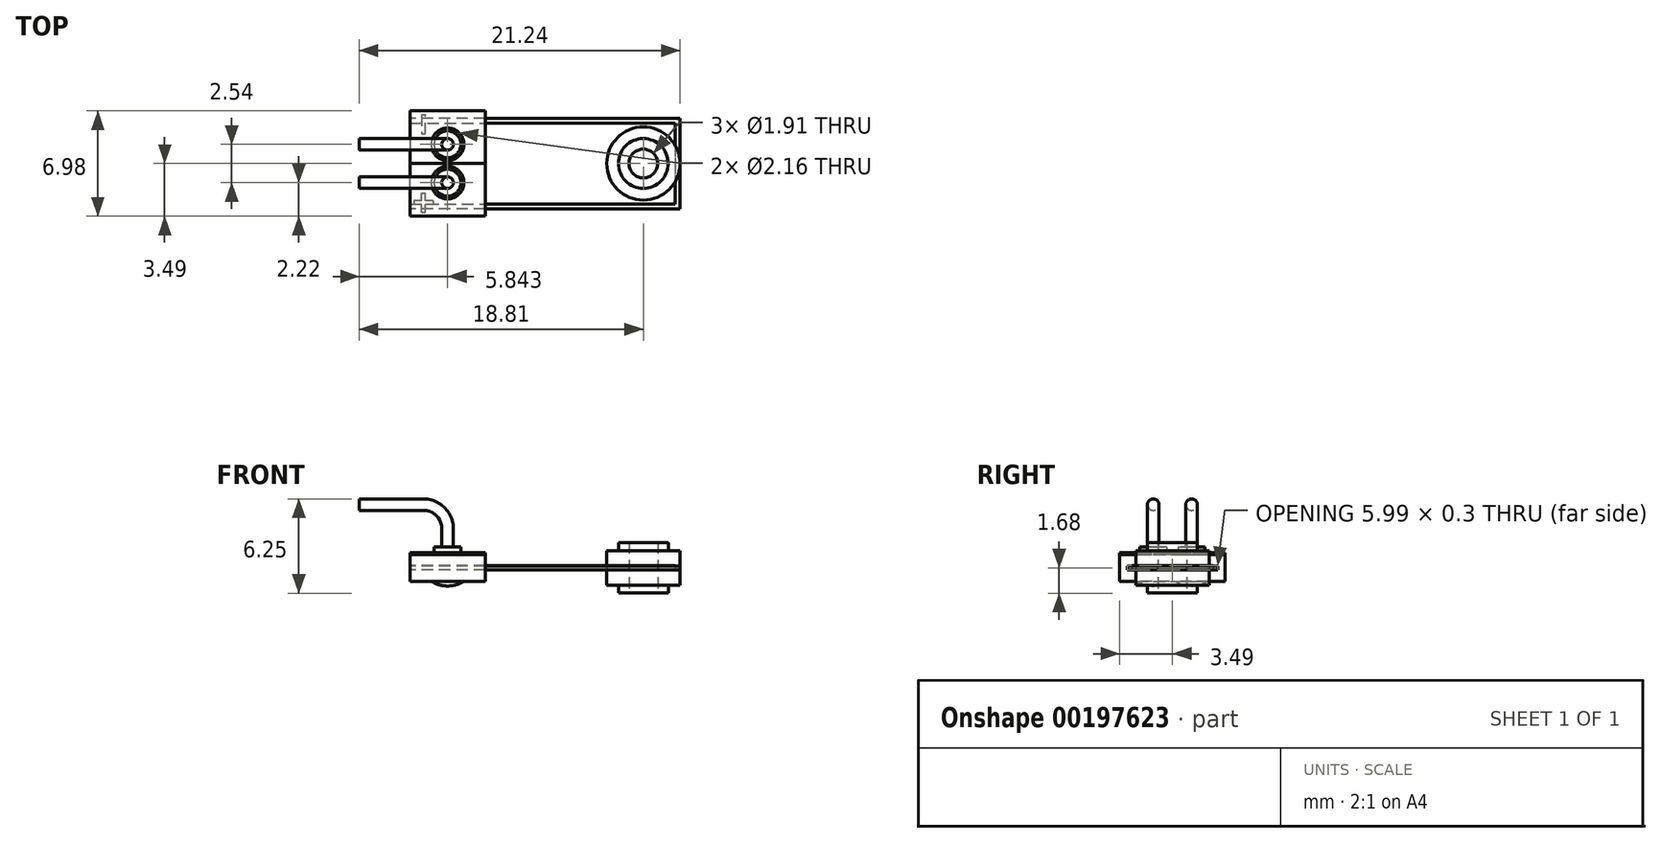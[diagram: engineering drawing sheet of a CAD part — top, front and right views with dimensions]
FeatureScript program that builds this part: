
annotation { "Feature Type Name" : "Feature", "Feature Type Description" : "" }
export const myFeature = defineFeature(function(context is Context, id is Id, definition is map)
    precondition{}
    {
        {
            var Q0;
            Q0=qCreatedBy(makeId("Top.planeOp"),FACE);
            var sketch = newSketch(context, id + "F0", { "sketchPlane" : qUnion([Q0])});
            skCircle(sketch, "E0", {"center": v(0, 0) * mm, "radius": 2.43 * mm});
            skCircle(sketch, "E1", {"center": v(0, 0) * mm, "radius": 1.65 * mm});
            skCircle(sketch, "E2", {"center": v(0, 0) * mm, "radius": 0.95 * mm});
            skSolve(sketch);
        }
        {
            var Q0;
            Q0=makeQuery(id+"F0.imprint","IMPRINT",FACE,{"disambiguationData":[TD([[makeQuery(id+"F0.imprint","IMPRINT",EDGE,{"derivedFrom":sQuery(id+"F0.wireOp",EDGE,"E0")}),1.0]])]});
            var Q1;
            Q1=makeQuery(id+"F0.imprint","IMPRINT",FACE,{"disambiguationData":[TD([[makeQuery(id+"F0.imprint","IMPRINT",EDGE,{"derivedFrom":sQuery(id+"F0.wireOp",EDGE,"E1")}),1.0]])]});
            extrude(context, id + "F1", {"entities" : qUnion([Q0, Q1]), "depth" : 1.14 * mm, "hasSecondDirection" : true, "secondDirectionOppositeDirection" : true, "secondDirectionDepth" : 1.14 * mm});
        }
        {
            var Q0;
            Q0=makeQuery(id+"F0.imprint","IMPRINT",FACE,{"disambiguationData":[TD([[makeQuery(id+"F0.imprint","IMPRINT",EDGE,{"derivedFrom":sQuery(id+"F0.wireOp",EDGE,"E1")}),1.0]])]});
            var Q1;
            Q1=sQuery(id+"F0.wireOp",EDGE,"E1");
            var Q2;
            Q2=sQuery(id+"F0.wireOp",EDGE,"E2");
            extrude(context, id + "F2", {"entities" : qUnion([Q0]), "operationType" : NewBodyOperationType.ADD, "surfaceEntities" : qUnion([Q1, Q2]), "endBound" : BoundingType.SYMMETRIC, "depth" : 3.35 * mm});
        }
        {
            var Q0;
            Q0=qCreatedBy(makeId("Top.planeOp"),FACE);
            var sketch = newSketch(context, id + "F3", { "sketchPlane" : qUnion([Q0])});
            skPoint(sketch, "E3", {"position": v(2.43, 0) * mm});
            skLineSegment(sketch, "E4.bottom", {"start": v(2.43, -3) * mm, "end": v(-15.46, -3) * mm});
            skLineSegment(sketch, "E4.top", {"start": v(2.43, 3) * mm, "end": v(-15.46, 3) * mm});
            skLineSegment(sketch, "E4.left", {"start": v(2.43, -3) * mm, "end": v(2.43, 3) * mm});
            skLineSegment(sketch, "E4.right", {"start": v(-15.46, -3) * mm, "end": v(-15.46, 3) * mm});
            skPoint(sketch, "E4.middle", {"position": v(-6.52, 0) * mm});
            skSolve(sketch);
        }
        {
            var Q0;
            Q0 = qSketchRegion(id + "F3", true);
            extrude(context, id + "F4", {"entities" : qUnion([Q0]), "endBound" : BoundingType.SYMMETRIC, "depth" : 0.25 * mm});
        }
        {
            var Q0;
            Q0=qCreatedBy(makeId("Top.planeOp"),FACE);
            var sketch = newSketch(context, id + "F5", { "sketchPlane" : qUnion([Q0])});
            skLineSegment(sketch, "E5.bottom", {"start": v(2.1, 2.68) * mm, "end": v(-15.46, 2.68) * mm});
            skLineSegment(sketch, "E5.top", {"start": v(2.1, -2.68) * mm, "end": v(-15.46, -2.68) * mm});
            skLineSegment(sketch, "E5.left", {"start": v(2.1, 2.68) * mm, "end": v(2.1, -2.68) * mm});
            skLineSegment(sketch, "E5.right", {"start": v(-15.46, 2.68) * mm, "end": v(-15.46, -2.68) * mm});
            skPoint(sketch, "E5.middle", {"position": v(-6.67, 0) * mm});
            skSolve(sketch);
        }
        {
            var Q0;
            Q0 = qSketchRegion(id + "F5", true);
            extrude(context, id + "F6", {"entities" : qUnion([Q0]), "endBound" : BoundingType.SYMMETRIC, "depth" : 0.3 * mm});
        }
        {
            var Q0;
            Q0=makeQuery(id+"F0.imprint","IMPRINT",FACE,{"disambiguationData":[TD([[makeQuery(id+"F0.imprint","IMPRINT",EDGE,{"derivedFrom":sQuery(id+"F0.wireOp",EDGE,"E2")}),1.0]])]});
            extrude(context, id + "F7", {"entities" : qUnion([Q0]), "operationType" : NewBodyOperationType.REMOVE, "endBound" : BoundingType.SYMMETRIC, "oppositeDirection" : true, "depth" : 25.4 * mm});
        }
        {
            var Q0;
            Q0=qCreatedBy(makeId("Top.planeOp"),FACE);
            var sketch = newSketch(context, id + "F8", { "sketchPlane" : qUnion([Q0])});
            skPoint(sketch, "E6.0", {"position": v(-15.46, 0) * mm});
            skLineSegment(sketch, "E7.bottom", {"start": v(-15.46, -3.5) * mm, "end": v(-10.48, -3.5) * mm});
            skLineSegment(sketch, "E7.top", {"start": v(-15.46, 3.5) * mm, "end": v(-10.48, 3.5) * mm});
            skLineSegment(sketch, "E7.left", {"start": v(-15.46, -3.5) * mm, "end": v(-15.46, 3.5) * mm});
            skLineSegment(sketch, "E7.right", {"start": v(-10.48, -3.5) * mm, "end": v(-10.48, 3.5) * mm});
            skPoint(sketch, "E7.middle", {"position": v(-12.97, 0) * mm});
            skSolve(sketch);
        }
        {
            var Q0;
            Q0=makeQuery(id+"F8.imprint","IMPRINT",FACE,{"disambiguationData":[TD([[makeQuery(id+"F8.imprint","IMPRINT",EDGE,{"derivedFrom":sQuery(id+"F8.wireOp",EDGE,"E7.bottom")}),1.0]])]});
            extrude(context, id + "F9", {"entities" : qUnion([Q0]), "endBound" : BoundingType.SYMMETRIC, "depth" : 1.78 * mm});
        }
        {
            var Q0;
            Q0=makeQuery(id+"F4.opExtrude","SWEPT_BODY",BODY,{"disambiguationData":[OSD([sQuery(id+"F3.wireOp",EDGE,"E4.bottom"),sQuery(id+"F3.wireOp",EDGE,"E4.top"),sQuery(id+"F3.wireOp",EDGE,"E4.left"),sQuery(id+"F3.wireOp",EDGE,"E4.right")])]});
            var Q1;
            Q1=makeQuery(id+"F6.opExtrude","SWEPT_BODY",BODY,{"disambiguationData":[OSD([sQuery(id+"F5.wireOp",EDGE,"E5.bottom"),sQuery(id+"F5.wireOp",EDGE,"E5.top"),sQuery(id+"F5.wireOp",EDGE,"E5.left"),sQuery(id+"F5.wireOp",EDGE,"E5.right")])]});
            var Q2;
            Q2=makeQuery(id+"F9.opExtrude","SWEPT_BODY",BODY,{"disambiguationData":[OSD([sQuery(id+"F8.wireOp",EDGE,"E7.bottom"),sQuery(id+"F8.wireOp",EDGE,"E7.top"),sQuery(id+"F8.wireOp",EDGE,"E7.left"),sQuery(id+"F8.wireOp",EDGE,"E7.right")])]});
            booleanBodies(context, id + "F10", {"operationType" : BooleanOperationType.SUBTRACTION, "tools" : qUnion([Q0, Q1]), "targets" : qUnion([Q2]), "keepTools" : true});
        }
        {
            var Q0;
            Q0=makeQuery(id+"F9.opExtrude","CAP_FACE",FACE,{"disambiguationData":[OSD([sQuery(id+"F8.wireOp",EDGE,"E7.bottom"),sQuery(id+"F8.wireOp",EDGE,"E7.top"),sQuery(id+"F8.wireOp",EDGE,"E7.left"),sQuery(id+"F8.wireOp",EDGE,"E7.right")])],"isStart":true});
            var sketch = newSketch(context, id + "F11", { "sketchPlane" : qUnion([Q0])});
            skPoint(sketch, "E8.0", {"position": v(0, 0) * mm});
            skPoint(sketch, "E9.0", {"position": v(-15.46, 0) * mm});
            skCircle(sketch, "E10.0", {"center": v(0, 0) * mm, "radius": 2.43 * mm});
            skPoint(sketch, "E11.middle", {"position": v(-12.97, 0) * mm});
            skPoint(sketch, "E11.middle.positionSnap0", {"position": v(-10.48, 0) * mm});
            skPoint(sketch, "E11.centerSnap0", {"position": v(-10.48, 0) * mm});
            skLineSegment(sketch, "E12", {"start": v(-15.46, 0) * mm, "end": v(-10.48, 0) * mm});
            skCircle(sketch, "E13", {"center": v(-12.97, 1.27) * mm, "radius": 1.08 * mm});
            skPoint(sketch, "E13.centerSnap0", {"position": v(-12.97, 0.25) * mm});
            skSolve(sketch);
        }
        {
            var Q0;
            Q0=qCreatedBy(makeId("Front.planeOp"),FACE);
            cPlane(context, id + "F12", {"entities" : qUnion([Q0]), "cplaneType" : CPlaneType.OFFSET, "offset" : 1.27 * mm, "width" : 152.4 * mm, "height" : 152.4 * mm});
        }
        {
            var Q0;
            Q0=qCreatedBy(id+"F12.planeOp",FACE);
            var sketch = newSketch(context, id + "F13", { "sketchPlane" : qUnion([Q0])});
            skLineSegment(sketch, "E14.0.0", {"start": v(-12.97, -0.89) * mm, "end": v(-14.05, -0.89) * mm});
            skArc(sketch, "E15", {"start": v(-14.05, -0.89) * mm, "mid": v(-13.53, -1.13) * mm, "end": v(-12.97, -1.2) * mm});
            skLineSegment(sketch, "E16", {"start": v(-12.97, -0.89) * mm, "end": v(-12.97, -1.2) * mm});
            skPoint(sketch, "E17.orphan", {"position": v(-11.89, -0.89) * mm});
            skSolve(sketch);
        }
        {
            var Q0;
            Q0 = qSketchRegion(id + "F13", true);
            var Q1;
            Q1=sQuery(id+"F13.wireOp",EDGE,"E16");
            revolve(context, id + "F14", {"entities" : qUnion([Q0]), "axis" : qUnion([Q1]), "revolveType" : RevolveType.FULL, "oppositeDirection" : true});
        }
        {
            var Q0;
            Q0=makeQuery(id+"F14.opRevolve","SWEPT_BODY",BODY,{"disambiguationData":[OSD([sQuery(id+"F13.wireOp",EDGE,"E14.0.0"),sQuery(id+"F13.wireOp",EDGE,"E15"),sQuery(id+"F13.wireOp",EDGE,"E16")])]});
            var Q1;
            Q1=qCreatedBy(makeId("Front.planeOp"),FACE);
            mirror(context, id + "F15", {"entities" : qUnion([Q0]), "mirrorPlane" : qUnion([Q1])});
        }
        {
            var Q0;
            Q0=makeQuery(id+"F9.opExtrude","CAP_FACE",FACE,{"disambiguationData":[OSD([sQuery(id+"F8.wireOp",EDGE,"E7.bottom"),sQuery(id+"F8.wireOp",EDGE,"E7.top"),sQuery(id+"F8.wireOp",EDGE,"E7.left"),sQuery(id+"F8.wireOp",EDGE,"E7.right")])],"isStart":false});
            var sketch = newSketch(context, id + "F16", { "sketchPlane" : qUnion([Q0])});
            skCircle(sketch, "E18.0", {"center": v(-12.97, -1.27) * mm, "radius": 1.08 * mm});
            skLineSegment(sketch, "E19.0", {"start": v(-15.46, 0) * mm, "end": v(-10.48, 0) * mm});
            skCircle(sketch, "E20", {"center": v(-12.97, -1.27) * mm, "radius": 0.89 * mm});
            skCircle(sketch, "E21", {"center": v(-12.97, -1.27) * mm, "radius": 0.5 * mm});
            skPoint(sketch, "E22", {"position": v(-12.46, -1.27) * mm});
            skPoint(sketch, "E23", {"position": v(-12.46, 0) * mm});
            skLineSegment(sketch, "E24", {"start": v(-12.46, -1.27) * mm, "end": v(-12.46, 0) * mm});
            skLineSegment(sketch, "E25", {"start": v(-12.46, -1.27) * mm, "end": v(-12.97, -1.27) * mm});
            skSolve(sketch);
        }
        {
            var Q0;
            Q0=makeQuery(id+"F16.imprint","IMPRINT",FACE,{"disambiguationData":[TD([[makeQuery(id+"F16.imprint","IMPRINT",EDGE,{"derivedFrom":sQuery(id+"F16.wireOp",EDGE,"E18.0")}),-1.0]])]});
            var Q1;
            Q1=makeQuery(id+"F16.imprint","IMPRINT",FACE,{"disambiguationData":[TD([[makeQuery(id+"F16.imprint","IMPRINT",EDGE,{"derivedFrom":sQuery(id+"F16.wireOp",EDGE,"E20")}),1.0]])]});
            var Q2;
            Q2=makeQuery(id+"F16.imprint","IMPRINT",FACE,{"disambiguationData":[TD([[makeQuery(id+"F16.imprint","IMPRINT",EDGE,{"derivedFrom":sQuery(id+"F16.wireOp",EDGE,"E21")}),1.0]])]});
            var Q3;
            Q3=sQuery(id+"F16.wireOp",EDGE,"E18.0");
            extrude(context, id + "F17", {"entities" : qUnion([Q0, Q1, Q2]), "surfaceEntities" : qUnion([Q3]), "depth" : 0.13 * mm});
        }
        {
            var Q0;
            Q0=makeQuery(id+"F17.opExtrude","SWEPT_BODY",BODY,{"disambiguationData":[OSD([sQuery(id+"F16.wireOp",EDGE,"E18.0")])]});
            var Q1;
            Q1=qCreatedBy(makeId("Front.planeOp"),FACE);
            mirror(context, id + "F18", {"entities" : qUnion([Q0]), "mirrorPlane" : qUnion([Q1])});
        }
        {
            var Q0;
            Q0=makeQuery(id+"F16.imprint","IMPRINT",FACE,{"disambiguationData":[TD([[makeQuery(id+"F16.imprint","IMPRINT",EDGE,{"derivedFrom":sQuery(id+"F16.wireOp",EDGE,"E20")}),1.0]])]});
            var Q1;
            Q1=makeQuery(id+"F16.imprint","IMPRINT",FACE,{"disambiguationData":[TD([[makeQuery(id+"F16.imprint","IMPRINT",EDGE,{"derivedFrom":sQuery(id+"F16.wireOp",EDGE,"E21")}),1.0]])]});
            extrude(context, id + "F19", {"entities" : qUnion([Q0, Q1]), "depth" : 0.5 * mm});
        }
        {
            var Q0;
            Q0=sQuery(id+"F16.wireOp",EDGE,"E24");
            var Q1;
            Q1=makeQuery(id+"F9.opExtrude","SWEPT_FACE",FACE,{"disambiguationData":[OSD([sQuery(id+"F8.wireOp",EDGE,"E7.left")])]});
            cPlane(context, id + "F20", {"entities" : qUnion([Q0, Q1]), "cplaneType" : CPlaneType.LINE_ANGLE, "offset" : 25.4 * mm, "angle" : 0 * degree, "width" : 152.4 * mm, "height" : 152.4 * mm});
        }
        {
            var Q0;
            Q0=sQuery(id+"F16.wireOp",EDGE,"E25");
            var Q1;
            Q1=qCreatedBy(makeId("Front.planeOp"),FACE);
            cPlane(context, id + "F21", {"entities" : qUnion([Q0, Q1]), "cplaneType" : CPlaneType.LINE_ANGLE, "offset" : 25.4 * mm, "angle" : 0 * degree, "width" : 152.4 * mm, "height" : 152.4 * mm});
        }
        {
            var Q0;
            Q0=qCreatedBy(id+"F21.planeOp",FACE);
            var sketch = newSketch(context, id + "F22", { "sketchPlane" : qUnion([Q0])});
            skPoint(sketch, "E26.0", {"position": v(12.97, 0.79) * mm});
            skLineSegment(sketch, "E27.0", {"start": v(12.08, 1.4) * mm, "end": v(13.86, 1.4) * mm});
            skPoint(sketch, "E28", {"position": v(18.8, 4.2) * mm});
            skPoint(sketch, "E29.endSnap0", {"position": v(12.97, 1.4) * mm});
            skLineSegment(sketch, "E30", {"start": v(18.8, 4.2) * mm, "end": v(14.55, 4.2) * mm});
            skLineSegment(sketch, "E31", {"start": v(12.97, 1.4) * mm, "end": v(12.97, 2.6) * mm});
            skPoint(sketch, "E32.visualSharp", {"position": v(12.97, 4.2) * mm});
            skArc(sketch, "E32.filletArc", {"start": v(14.55, 4.2) * mm, "mid": v(13.43, 3.73) * mm, "end": v(12.97, 2.6) * mm});
            skSolve(sketch);
        }
        {
            var Q0;
            Q0=makeQuery(id+"F19.opExtrude","CAP_FACE",FACE,{"disambiguationData":[OSD([sQuery(id+"F16.wireOp",EDGE,"E20")])],"isStart":false});
            var sketch = newSketch(context, id + "F23", { "sketchPlane" : qUnion([Q0])});
            skCircle(sketch, "E33", {"center": v(-12.97, -1.27) * mm, "radius": 0.38 * mm});
            skSolve(sketch);
        }
        {
            var Q0;
            Q0=makeQuery(id+"F23.imprint","IMPRINT",FACE,{"disambiguationData":[TD([[makeQuery(id+"F23.imprint","IMPRINT",EDGE,{"derivedFrom":sQuery(id+"F23.wireOp",EDGE,"E33")}),1.0]])]});
            var Q1;
            Q1=sQuery(id+"F22.wireOp",EDGE,"E31");
            var Q2;
            Q2=sQuery(id+"F22.wireOp",EDGE,"E32.filletArc");
            var Q3;
            Q3=sQuery(id+"F22.wireOp",EDGE,"E30");
            sweep(context, id + "F24", {"operationType" : NewBodyOperationType.ADD, "profiles" : qUnion([Q0]), "path" : qUnion([Q1, Q2, Q3])});
        }
        {
            var Q0;
            Q0=makeQuery(id+"F19.opExtrude","SWEPT_BODY",BODY,{"disambiguationData":[OSD([sQuery(id+"F16.wireOp",EDGE,"E20")])]});
            var Q1;
            Q1=qCreatedBy(makeId("Front.planeOp"),FACE);
            mirror(context, id + "F25", {"entities" : qUnion([Q0]), "mirrorPlane" : qUnion([Q1])});
        }
        {
            var Q0;
            {var subQ2=sQuery(id+"F11.wireOp",EDGE,"E12");Q0=makeQuery(id+"F11.imprint","IMPRINT",FACE,{"disambiguationData":[TD([[makeQuery(id+"F11.imprint","IMPRINT",EDGE,{"derivedFrom":subQ2}),1.0]])]});}
            var sketch = newSketch(context, id + "F26", { "sketchPlane" : qUnion([Q0])});
            skLineSegment(sketch, "E34.bottom", {"start": v(-14.7, 3.24) * mm, "end": v(-14.44, 3.24) * mm});
            skLineSegment(sketch, "E34.top", {"start": v(-14.7, 1.97) * mm, "end": v(-14.44, 1.97) * mm});
            skLineSegment(sketch, "E34.left", {"start": v(-14.7, 3.24) * mm, "end": v(-14.7, 2.73) * mm});
            skLineSegment(sketch, "E34.right", {"start": v(-14.44, 3.24) * mm, "end": v(-14.44, 2.73) * mm});
            skPoint(sketch, "E35", {"position": v(-14.7, 2.6) * mm});
            skPoint(sketch, "E36", {"position": v(-14.44, 2.6) * mm});
            skPoint(sketch, "E37", {"position": v(-14.57, 2.6) * mm});
            skLineSegment(sketch, "E38.bottom", {"start": v(-13.93, 2.48) * mm, "end": v(-14.44, 2.48) * mm});
            skLineSegment(sketch, "E38.top", {"start": v(-13.93, 2.73) * mm, "end": v(-14.44, 2.73) * mm});
            skLineSegment(sketch, "E38.left", {"start": v(-13.93, 2.48) * mm, "end": v(-13.93, 2.73) * mm});
            skLineSegment(sketch, "E38.right", {"start": v(-15.2, 2.48) * mm, "end": v(-15.2, 2.73) * mm});
            skLineSegment(sketch, "E39.trimOffspring", {"start": v(-14.7, 2.73) * mm, "end": v(-15.2, 2.73) * mm});
            skLineSegment(sketch, "E40.trimOffspring", {"start": v(-14.7, 2.48) * mm, "end": v(-14.7, 1.97) * mm});
            skLineSegment(sketch, "E41.trimOffspring", {"start": v(-14.44, 2.48) * mm, "end": v(-14.44, 1.97) * mm});
            skLineSegment(sketch, "E42.trimOffspring", {"start": v(-14.7, 2.48) * mm, "end": v(-15.2, 2.48) * mm});
            skLineSegment(sketch, "E43.MirrorCS", {"start": v(-14.7, -1.97) * mm, "end": v(-14.44, -1.97) * mm});
            skLineSegment(sketch, "E44.MirrorCS", {"start": v(-14.7, -3.24) * mm, "end": v(-14.44, -3.24) * mm});
            skPoint(sketch, "E45.MirrorP", {"position": v(-14.57, -2.6) * mm});
            skPoint(sketch, "E46.MirrorP", {"position": v(-14.44, -2.6) * mm});
            skPoint(sketch, "E47.MirrorP", {"position": v(-14.7, -2.6) * mm});
            skPoint(sketch, "E48.MirrorCS.start.orphan", {"position": v(-14.7, -2.48) * mm});
            skPoint(sketch, "E49.MirrorCS.end.orphan", {"position": v(-15.2, -2.73) * mm});
            skPoint(sketch, "E49.MirrorCS.start.orphan", {"position": v(-15.2, -2.48) * mm});
            skPoint(sketch, "E50.MirrorCS.end.orphan", {"position": v(-14.44, -2.48) * mm});
            skPoint(sketch, "E51.MirrorCS.end.orphan", {"position": v(-13.93, -2.73) * mm});
            skPoint(sketch, "E51.MirrorCS.start.orphan", {"position": v(-13.93, -2.48) * mm});
            skPoint(sketch, "E52.MirrorCS.end.orphan", {"position": v(-14.7, -2.73) * mm});
            skPoint(sketch, "E53.MirrorCS.end.orphan", {"position": v(-14.44, -2.73) * mm});
            skLineSegment(sketch, "E54", {"start": v(-14.7, -3.24) * mm, "end": v(-14.7, -1.97) * mm});
            skLineSegment(sketch, "E55", {"start": v(-14.44, -1.97) * mm, "end": v(-14.44, -3.24) * mm});
            skSolve(sketch);
        }
        {
            var Q0;
            Q0 = qSketchRegion(id + "F26", true);
            extrude(context, id + "F27", {"entities" : qUnion([Q0]), "depth" : 0.03 * mm});
        }
    });
